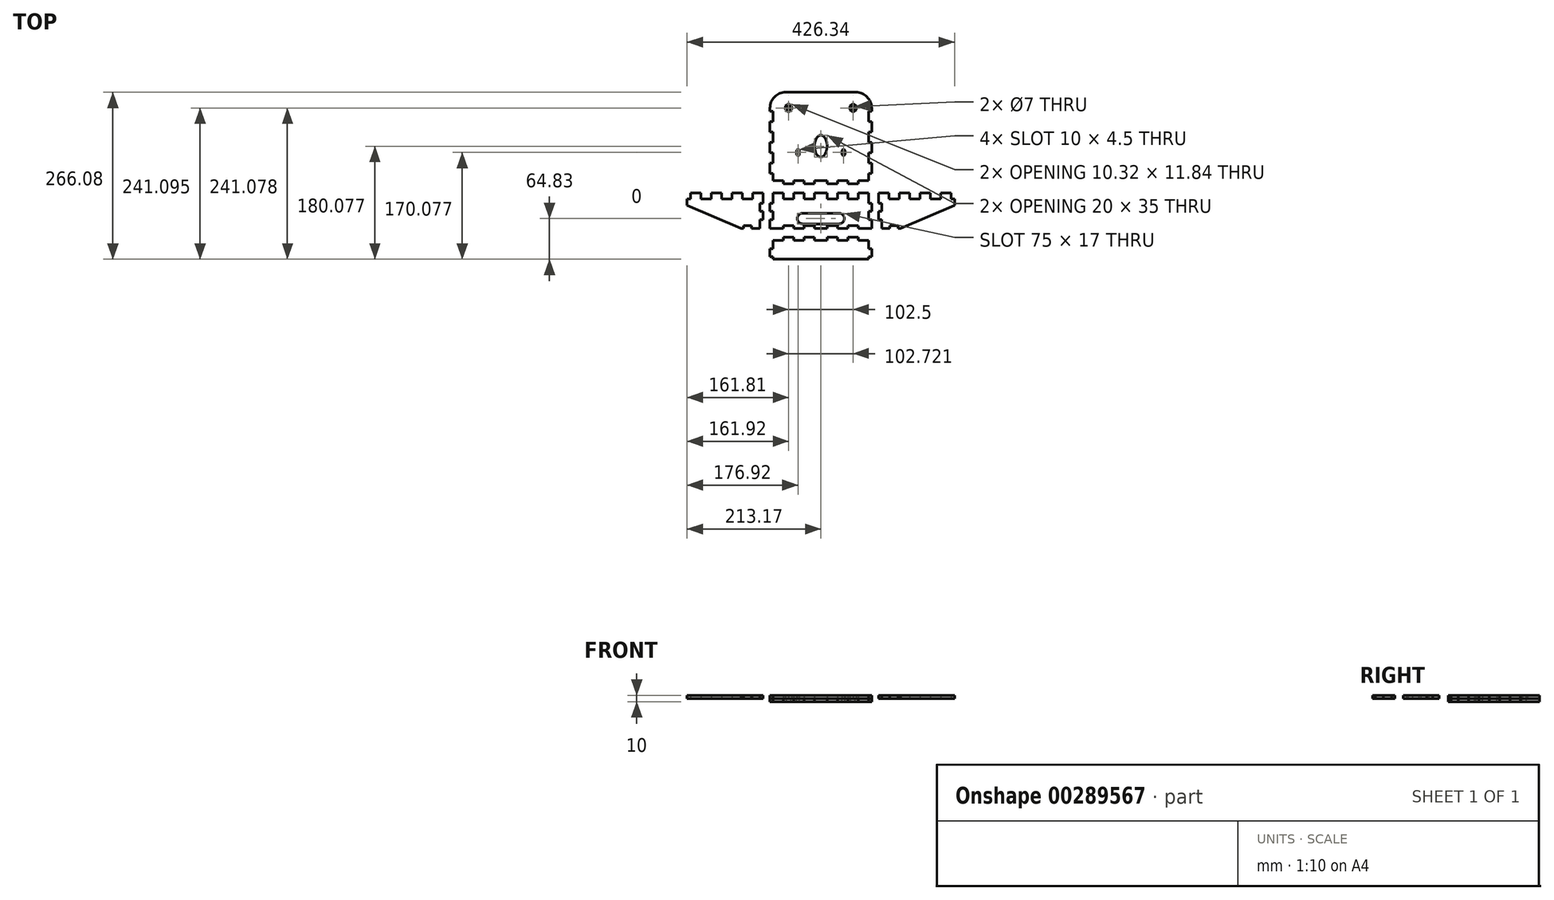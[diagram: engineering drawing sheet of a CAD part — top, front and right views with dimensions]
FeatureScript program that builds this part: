
annotation { "Feature Type Name" : "Feature", "Feature Type Description" : "" }
export const myFeature = defineFeature(function(context is Context, id is Id, definition is map)
    precondition{}
    {
        {
            assignVariable(context, id + "F0", {"name" : "plywoodThickness", "anyValue" : 5});
        }
        {
            var Q0;
            Q0=qCreatedBy(makeId("Top.planeOp"),FACE);
            var sketch = newSketch(context, id + "F1", { "sketchPlane" : qUnion([Q0])});
            skLineSegment(sketch, "E0.top", {"start": v(76, 28.5) * mm, "end": v(59.5, 28.5) * mm});
            skLineSegment(sketch, "E0.left", {"start": v(81, -28.5) * mm, "end": v(81, -14) * mm});
            skPoint(sketch, "E0.middle", {"position": v(0, 0) * mm});
            skLineSegment(sketch, "E1", {"start": v(0, -28.5) * mm, "end": v(0, -21) * mm, "construction": true});
            skLineSegment(sketch, "E2", {"start": v(0, -21) * mm, "end": v(29, -21) * mm});
            skLineSegment(sketch, "E3", {"start": v(37.5, -12.5) * mm, "end": v(37.5, -12.5) * mm});
            skLineSegment(sketch, "E4", {"start": v(29, -4) * mm, "end": v(0, -4) * mm});
            skPoint(sketch, "E5.visualSharp", {"position": v(37.5, -4) * mm});
            skArc(sketch, "E5.filletArc", {"start": v(37.5, -12.5) * mm, "mid": v(35.01, -6.49) * mm, "end": v(29, -4) * mm});
            skPoint(sketch, "E6.visualSharp", {"position": v(37.5, -21) * mm});
            skArc(sketch, "E6.filletArc", {"start": v(29, -21) * mm, "mid": v(35.01, -18.51) * mm, "end": v(37.5, -12.5) * mm});
            skLineSegment(sketch, "E7", {"start": v(59.5, -42.33) * mm, "end": v(43, -42.33) * mm});
            skLineSegment(sketch, "E8", {"start": v(81, -60.33) * mm, "end": v(81, -73.33) * mm});
            skLineSegment(sketch, "E9", {"start": v(76, -77.33) * mm, "end": v(0, -77.33) * mm});
            skLineSegment(sketch, "E10", {"start": v(92.17, -14) * mm, "end": v(92.17, -1) * mm});
            skLineSegment(sketch, "E11", {"start": v(97.17, -28.5) * mm, "end": v(110.17, -28.5) * mm});
            skPoint(sketch, "E12", {"position": v(0, 28.5) * mm});
            skLineSegment(sketch, "E13", {"start": v(59.5, 42.75) * mm, "end": v(43, 42.75) * mm});
            skLineSegment(sketch, "E14", {"start": v(81, 59.25) * mm, "end": v(81, 75.75) * mm});
            skLineSegment(sketch, "E15", {"start": v(56, 188.75) * mm, "end": v(0, 188.75) * mm});
            skLineSegment(sketch, "E16", {"start": v(59.5, 28.5) * mm, "end": v(59.5, 18.5) * mm});
            skLineSegment(sketch, "E17", {"start": v(59.5, 18.5) * mm, "end": v(43, 18.5) * mm});
            skLineSegment(sketch, "E18", {"start": v(43, 18.5) * mm, "end": v(43, 28.5) * mm});
            skLineSegment(sketch, "E19.trimOffspring", {"start": v(43, 28.5) * mm, "end": v(26.5, 28.5) * mm});
            skLineSegment(sketch, "E20", {"start": v(76, 28.5) * mm, "end": v(76, 18.5) * mm});
            skLineSegment(sketch, "E21.1.0.1", {"start": v(26.5, 28.5) * mm, "end": v(26.5, 18.5) * mm});
            skLineSegment(sketch, "E21.1.0.2", {"start": v(26.5, 18.5) * mm, "end": v(10, 18.5) * mm});
            skLineSegment(sketch, "E21.1.0.3", {"start": v(10, 18.5) * mm, "end": v(10, 28.5) * mm});
            skLineSegment(sketch, "E21.direction1", {"start": v(43, 18.5) * mm, "end": v(10, 18.5) * mm, "construction": true});
            skLineSegment(sketch, "E22.trimOffspring", {"start": v(10, 28.5) * mm, "end": v(0, 28.5) * mm});
            skLineSegment(sketch, "E23", {"start": v(59.5, 42.75) * mm, "end": v(59.5, 47.75) * mm});
            skLineSegment(sketch, "E24", {"start": v(59.5, 47.75) * mm, "end": v(76, 47.75) * mm});
            skLineSegment(sketch, "E25", {"start": v(43, 42.75) * mm, "end": v(43, 47.75) * mm});
            skLineSegment(sketch, "E26", {"start": v(43, 47.75) * mm, "end": v(26.5, 47.75) * mm});
            skLineSegment(sketch, "E27", {"start": v(26.5, 47.75) * mm, "end": v(26.5, 42.75) * mm});
            skLineSegment(sketch, "E28", {"start": v(26.5, 42.75) * mm, "end": v(10, 42.75) * mm});
            skLineSegment(sketch, "E29", {"start": v(10, 42.75) * mm, "end": v(10, 47.75) * mm});
            skLineSegment(sketch, "E30", {"start": v(10, 47.75) * mm, "end": v(0, 47.75) * mm});
            skLineSegment(sketch, "E31", {"start": v(76, 47.75) * mm, "end": v(76, 59.25) * mm});
            skLineSegment(sketch, "E32", {"start": v(76, 59.25) * mm, "end": v(81, 59.25) * mm});
            skLineSegment(sketch, "E33", {"start": v(81, 188.75) * mm, "end": v(81, 163.75) * mm, "construction": true});
            skLineSegment(sketch, "E34", {"start": v(81, 75.75) * mm, "end": v(76, 75.75) * mm});
            skLineSegment(sketch, "E35", {"start": v(76, 75.75) * mm, "end": v(76, 92.25) * mm});
            skLineSegment(sketch, "E36", {"start": v(76, 59.25) * mm, "end": v(76, 75.75) * mm, "construction": true});
            skLineSegment(sketch, "E37", {"start": v(76, 92.25) * mm, "end": v(81, 92.25) * mm});
            skLineSegment(sketch, "E38.trimOffspring", {"start": v(81, 92.25) * mm, "end": v(81, 108.75) * mm});
            skLineSegment(sketch, "E39.0.1.1", {"start": v(81, 108.75) * mm, "end": v(76, 108.75) * mm});
            skLineSegment(sketch, "E39.0.1.2", {"start": v(76, 108.75) * mm, "end": v(76, 125.25) * mm});
            skLineSegment(sketch, "E39.0.1.3", {"start": v(76, 125.25) * mm, "end": v(81, 125.25) * mm});
            skLineSegment(sketch, "E39.0.2.0", {"start": v(81, 125.25) * mm, "end": v(81, 141.75) * mm});
            skLineSegment(sketch, "E39.0.2.1", {"start": v(81, 141.75) * mm, "end": v(76, 141.75) * mm});
            skLineSegment(sketch, "E39.0.2.2", {"start": v(76, 141.75) * mm, "end": v(76, 158.25) * mm});
            skLineSegment(sketch, "E39.0.2.3", {"start": v(76, 158.25) * mm, "end": v(81, 158.25) * mm});
            skLineSegment(sketch, "E39.direction1", {"start": v(81, 59.25) * mm, "end": v(106, 59.25) * mm, "construction": true});
            skLineSegment(sketch, "E39.direction2", {"start": v(81, 59.25) * mm, "end": v(81, 92.25) * mm, "construction": true});
            skLineSegment(sketch, "E40.trimOffspring", {"start": v(81, 158.25) * mm, "end": v(81, 163.75) * mm});
            skLineSegment(sketch, "E41", {"start": v(92.17, 28.5) * mm, "end": v(108.67, 28.5) * mm});
            skLineSegment(sketch, "E42", {"start": v(108.67, 28.5) * mm, "end": v(108.67, 18.5) * mm});
            skLineSegment(sketch, "E43", {"start": v(108.67, 18.5) * mm, "end": v(125.17, 18.5) * mm});
            skLineSegment(sketch, "E44", {"start": v(125.17, 18.5) * mm, "end": v(125.17, 28.5) * mm});
            skLineSegment(sketch, "E45", {"start": v(97.17, -28.5) * mm, "end": v(110.17, -28.5) * mm, "construction": true});
            skLineSegment(sketch, "E46", {"start": v(213.17, -28.5) * mm, "end": v(213.17, 18.5) * mm, "construction": true});
            skLineSegment(sketch, "E47.1.0.0", {"start": v(158.17, 18.5) * mm, "end": v(158.17, 28.5) * mm});
            skLineSegment(sketch, "E47.1.0.1", {"start": v(125.17, 28.5) * mm, "end": v(141.67, 28.5) * mm});
            skLineSegment(sketch, "E47.1.0.2", {"start": v(141.67, 18.5) * mm, "end": v(158.17, 18.5) * mm});
            skLineSegment(sketch, "E47.1.0.3", {"start": v(141.67, 28.5) * mm, "end": v(141.67, 18.5) * mm});
            skLineSegment(sketch, "E47.2.0.0", {"start": v(191.17, 18.5) * mm, "end": v(191.17, 28.5) * mm});
            skLineSegment(sketch, "E47.2.0.1", {"start": v(158.17, 28.5) * mm, "end": v(174.67, 28.5) * mm});
            skLineSegment(sketch, "E47.2.0.2", {"start": v(174.67, 18.5) * mm, "end": v(191.17, 18.5) * mm});
            skLineSegment(sketch, "E47.2.0.3", {"start": v(174.67, 28.5) * mm, "end": v(174.67, 18.5) * mm});
            skLineSegment(sketch, "E47.3.0.1", {"start": v(191.17, 28.5) * mm, "end": v(207.67, 28.5) * mm});
            skLineSegment(sketch, "E47.3.0.2", {"start": v(207.67, 18.5) * mm, "end": v(213.17, 18.5) * mm});
            skLineSegment(sketch, "E47.3.0.3", {"start": v(207.67, 28.5) * mm, "end": v(207.67, 18.5) * mm});
            skLineSegment(sketch, "E47.direction1", {"start": v(92.17, 28.5) * mm, "end": v(125.17, 28.5) * mm, "construction": true});
            skLineSegment(sketch, "E48", {"start": v(213.17, 18.5) * mm, "end": v(213.17, 8.5) * mm});
            skLineSegment(sketch, "E49", {"start": v(213.17, 8.5) * mm, "end": v(127.17, -28.5) * mm});
            skLineSegment(sketch, "E50", {"start": v(76, 28.5) * mm, "end": v(76, 12) * mm});
            skLineSegment(sketch, "E51", {"start": v(76, 12) * mm, "end": v(81, 12) * mm});
            skLineSegment(sketch, "E52", {"start": v(92.17, 12) * mm, "end": v(97.17, 12) * mm});
            skLineSegment(sketch, "E53", {"start": v(97.17, 12) * mm, "end": v(97.17, -1) * mm});
            skLineSegment(sketch, "E54", {"start": v(97.17, -1) * mm, "end": v(92.17, -1) * mm});
            skLineSegment(sketch, "E55.trimOffspring", {"start": v(92.17, 12) * mm, "end": v(92.17, 28.5) * mm});
            skLineSegment(sketch, "E56", {"start": v(81, -1) * mm, "end": v(76, -1) * mm});
            skLineSegment(sketch, "E57", {"start": v(76, -1) * mm, "end": v(76, -14) * mm});
            skLineSegment(sketch, "E58", {"start": v(76, -14) * mm, "end": v(81, -14) * mm});
            skLineSegment(sketch, "E59.trimOffspring", {"start": v(81, -1) * mm, "end": v(81, 12) * mm});
            skLineSegment(sketch, "E60", {"start": v(92.17, -14) * mm, "end": v(97.17, -14) * mm});
            skLineSegment(sketch, "E61", {"start": v(97.17, -14) * mm, "end": v(97.17, -28.5) * mm});
            skLineSegment(sketch, "E62", {"start": v(110.17, -28.5) * mm, "end": v(110.17, -23.5) * mm});
            skLineSegment(sketch, "E63", {"start": v(110.17, -23.5) * mm, "end": v(123.17, -23.5) * mm});
            skLineSegment(sketch, "E64", {"start": v(123.17, -23.5) * mm, "end": v(123.17, -28.5) * mm});
            skLineSegment(sketch, "E65.trimOffspring", {"start": v(123.17, -28.5) * mm, "end": v(213.17, -28.5) * mm, "construction": true});
            skLineSegment(sketch, "E66.trimOffspring", {"start": v(123.17, -28.5) * mm, "end": v(127.17, -28.5) * mm});
            skLineSegment(sketch, "E67", {"start": v(76, -47.33) * mm, "end": v(76, -60.33) * mm});
            skLineSegment(sketch, "E68", {"start": v(76, -60.33) * mm, "end": v(81, -60.33) * mm});
            skLineSegment(sketch, "E69", {"start": v(81, -73.33) * mm, "end": v(76, -73.33) * mm});
            skLineSegment(sketch, "E70", {"start": v(76, -73.33) * mm, "end": v(76, -77.33) * mm});
            skLineSegment(sketch, "E71", {"start": v(59.5, -28.5) * mm, "end": v(59.5, -23.5) * mm});
            skLineSegment(sketch, "E72", {"start": v(59.5, -23.5) * mm, "end": v(43, -23.5) * mm});
            skLineSegment(sketch, "E73", {"start": v(43, -23.5) * mm, "end": v(43, -28.5) * mm});
            skLineSegment(sketch, "E74", {"start": v(26.5, -28.5) * mm, "end": v(26.5, -23.5) * mm});
            skLineSegment(sketch, "E75", {"start": v(26.5, -23.5) * mm, "end": v(10, -23.5) * mm});
            skLineSegment(sketch, "E76", {"start": v(10, -23.5) * mm, "end": v(10, -28.5) * mm});
            skLineSegment(sketch, "E77.trimOffspring", {"start": v(43, -28.5) * mm, "end": v(26.5, -28.5) * mm});
            skLineSegment(sketch, "E78.trimOffspring", {"start": v(10, -28.5) * mm, "end": v(0, -28.5) * mm});
            skLineSegment(sketch, "E79", {"start": v(59.5, -28.5) * mm, "end": v(81, -28.5) * mm});
            skLineSegment(sketch, "E80", {"start": v(59.5, -42.33) * mm, "end": v(59.5, -47.33) * mm});
            skLineSegment(sketch, "E81", {"start": v(59.5, -47.33) * mm, "end": v(76, -47.33) * mm});
            skLineSegment(sketch, "E82", {"start": v(43, -42.33) * mm, "end": v(43, -47.33) * mm});
            skLineSegment(sketch, "E83", {"start": v(43, -47.33) * mm, "end": v(26.5, -47.33) * mm});
            skLineSegment(sketch, "E84", {"start": v(26.5, -47.33) * mm, "end": v(26.5, -42.33) * mm});
            skLineSegment(sketch, "E85", {"start": v(10, -42.33) * mm, "end": v(10, -47.33) * mm});
            skLineSegment(sketch, "E86", {"start": v(10, -47.33) * mm, "end": v(0, -47.33) * mm});
            skLineSegment(sketch, "E87.trimOffspring", {"start": v(26.5, -42.33) * mm, "end": v(10, -42.33) * mm});
            skLineSegment(sketch, "E88", {"start": v(0, -85.94) * mm, "end": v(0, 158.23) * mm, "construction": true});
            skLineSegment(sketch, "E89.MirrorCS", {"start": v(-76, 59.25) * mm, "end": v(-81, 59.25) * mm});
            skLineSegment(sketch, "E90.MirrorCS", {"start": v(-76, 92.25) * mm, "end": v(-81, 92.25) * mm});
            skLineSegment(sketch, "E91.MirrorCS", {"start": v(-59.5, 42.75) * mm, "end": v(-59.5, 47.75) * mm});
            skLineSegment(sketch, "E92.MirrorCS", {"start": v(-43, 42.75) * mm, "end": v(-43, 47.75) * mm});
            skLineSegment(sketch, "E93.MirrorCS", {"start": v(-81, 108.75) * mm, "end": v(-76, 108.75) * mm});
            skLineSegment(sketch, "E94.MirrorCS", {"start": v(-59.5, -28.5) * mm, "end": v(-59.5, -23.5) * mm});
            skLineSegment(sketch, "E95.MirrorCS", {"start": v(-76, -73.33) * mm, "end": v(-76, -77.33) * mm});
            skLineSegment(sketch, "E96.MirrorCS", {"start": v(-76, 158.25) * mm, "end": v(-81, 158.25) * mm});
            skLineSegment(sketch, "E97.MirrorCS", {"start": v(-10, -42.33) * mm, "end": v(-10, -47.33) * mm});
            skLineSegment(sketch, "E98.MirrorCS", {"start": v(-81, -73.33) * mm, "end": v(-76, -73.33) * mm});
            skLineSegment(sketch, "E99.MirrorCS", {"start": v(-81, -1) * mm, "end": v(-76, -1) * mm});
            skLineSegment(sketch, "E100.MirrorCS", {"start": v(-10, 42.75) * mm, "end": v(-10, 47.75) * mm});
            skLineSegment(sketch, "E101.MirrorCS", {"start": v(-81, 141.75) * mm, "end": v(-76, 141.75) * mm});
            skLineSegment(sketch, "E102.MirrorCS", {"start": v(-76, -14) * mm, "end": v(-81, -14) * mm});
            skLineSegment(sketch, "E103.MirrorCS", {"start": v(-43, -42.33) * mm, "end": v(-43, -47.33) * mm});
            skLineSegment(sketch, "E104.MirrorCS", {"start": v(-81, -60.33) * mm, "end": v(-81, -73.33) * mm});
            skLineSegment(sketch, "E105.MirrorCS", {"start": v(-43, -23.5) * mm, "end": v(-43, -28.5) * mm});
            skLineSegment(sketch, "E106.MirrorCS", {"start": v(-26.5, 47.75) * mm, "end": v(-26.5, 42.75) * mm});
            skLineSegment(sketch, "E107.MirrorCS", {"start": v(-76, 12) * mm, "end": v(-81, 12) * mm});
            skLineSegment(sketch, "E108.MirrorCS", {"start": v(-26.5, -28.5) * mm, "end": v(-26.5, -23.5) * mm});
            skLineSegment(sketch, "E109.MirrorCS", {"start": v(-59.5, -42.33) * mm, "end": v(-59.5, -47.33) * mm});
            skLineSegment(sketch, "E110.MirrorCS", {"start": v(-76, 125.25) * mm, "end": v(-81, 125.25) * mm});
            skLineSegment(sketch, "E111.MirrorCS", {"start": v(-76, -60.33) * mm, "end": v(-81, -60.33) * mm});
            skLineSegment(sketch, "E112.MirrorCS", {"start": v(-10, -23.5) * mm, "end": v(-10, -28.5) * mm});
            skLineSegment(sketch, "E113.MirrorCS", {"start": v(-26.5, -47.33) * mm, "end": v(-26.5, -42.33) * mm});
            skLineSegment(sketch, "E114.MirrorCS", {"start": v(-81, 75.75) * mm, "end": v(-76, 75.75) * mm});
            skLineSegment(sketch, "E115.MirrorCS", {"start": v(-81, 92.25) * mm, "end": v(-81, 108.75) * mm});
            skLineSegment(sketch, "E116.MirrorCS", {"start": v(-76, 28.5) * mm, "end": v(-76, 18.5) * mm});
            skLineSegment(sketch, "E117.MirrorCS", {"start": v(-81, 59.25) * mm, "end": v(-81, 75.75) * mm});
            skLineSegment(sketch, "E118.MirrorCS", {"start": v(-81, 158.25) * mm, "end": v(-81, 163.75) * mm});
            skLineSegment(sketch, "E119.MirrorCS", {"start": v(-76, 28.5) * mm, "end": v(-59.5, 28.5) * mm});
            skLineSegment(sketch, "E120.MirrorCS", {"start": v(-81, 125.25) * mm, "end": v(-81, 141.75) * mm});
            skLineSegment(sketch, "E121.MirrorCS", {"start": v(-43, 28.5) * mm, "end": v(-26.5, 28.5) * mm});
            skLineSegment(sketch, "E122.MirrorCS", {"start": v(-26.5, 42.75) * mm, "end": v(-10, 42.75) * mm});
            skLineSegment(sketch, "E123.MirrorCS", {"start": v(-26.5, 18.5) * mm, "end": v(-10, 18.5) * mm});
            skLineSegment(sketch, "E124.MirrorCS", {"start": v(-76, 28.5) * mm, "end": v(-76, 12) * mm});
            skLineSegment(sketch, "E125.MirrorCS", {"start": v(-76, -1) * mm, "end": v(-76, -14) * mm});
            skLineSegment(sketch, "E126.MirrorCS", {"start": v(-10, -28.5) * mm, "end": v(0, -28.5) * mm});
            skLineSegment(sketch, "E127.MirrorCS", {"start": v(-10, 28.5) * mm, "end": v(0, 28.5) * mm});
            skPoint(sketch, "E128.MirrorP", {"position": v(-37.5, -4) * mm});
            skLineSegment(sketch, "E129.MirrorCS", {"start": v(-59.5, -28.5) * mm, "end": v(-81, -28.5) * mm});
            skLineSegment(sketch, "E130.MirrorCS", {"start": v(-81, 59.25) * mm, "end": v(-106, 59.25) * mm, "construction": true});
            skLineSegment(sketch, "E131.MirrorCS", {"start": v(-76, 47.75) * mm, "end": v(-76, 59.25) * mm});
            skLineSegment(sketch, "E132.MirrorCS", {"start": v(-59.5, -47.33) * mm, "end": v(-76, -47.33) * mm});
            skLineSegment(sketch, "E133.MirrorCS", {"start": v(-59.5, 47.75) * mm, "end": v(-76, 47.75) * mm});
            skLineSegment(sketch, "E134.MirrorCS", {"start": v(-59.5, -23.5) * mm, "end": v(-43, -23.5) * mm});
            skLineSegment(sketch, "E135.MirrorCS", {"start": v(-43, 18.5) * mm, "end": v(-43, 28.5) * mm});
            skLineSegment(sketch, "E136.MirrorCS", {"start": v(-43, -28.5) * mm, "end": v(-26.5, -28.5) * mm});
            skLineSegment(sketch, "E137.MirrorCS", {"start": v(-76, 59.25) * mm, "end": v(-76, 75.75) * mm, "construction": true});
            skLineSegment(sketch, "E138.MirrorCS", {"start": v(-43, 18.5) * mm, "end": v(-10, 18.5) * mm, "construction": true});
            skLineSegment(sketch, "E139.MirrorCS", {"start": v(-76, -77.33) * mm, "end": v(0, -77.33) * mm});
            skArc(sketch, "E140.MirrorCS", {"start": v(-29, -21) * mm, "mid": v(-35.01, -18.51) * mm, "end": v(-37.5, -12.5) * mm});
            skLineSegment(sketch, "E141.MirrorCS", {"start": v(-10, 47.75) * mm, "end": v(0, 47.75) * mm});
            skLineSegment(sketch, "E142.MirrorCS", {"start": v(-10, -47.33) * mm, "end": v(0, -47.33) * mm});
            skLineSegment(sketch, "E143.MirrorCS", {"start": v(-29, -4) * mm, "end": v(0, -4) * mm});
            skLineSegment(sketch, "E144.MirrorCS", {"start": v(0, -21) * mm, "end": v(-29, -21) * mm});
            skLineSegment(sketch, "E145.MirrorCS", {"start": v(-76, 141.75) * mm, "end": v(-76, 158.25) * mm});
            skLineSegment(sketch, "E146.MirrorCS", {"start": v(-59.5, 28.5) * mm, "end": v(-59.5, 18.5) * mm});
            skLineSegment(sketch, "E147.MirrorCS", {"start": v(-59.5, 18.5) * mm, "end": v(-43, 18.5) * mm});
            skLineSegment(sketch, "E148.MirrorCS", {"start": v(-10, 18.5) * mm, "end": v(-10, 28.5) * mm});
            skLineSegment(sketch, "E149.MirrorCS", {"start": v(-56, 188.75) * mm, "end": v(0, 188.75) * mm});
            skLineSegment(sketch, "E150.MirrorCS", {"start": v(-76, -47.33) * mm, "end": v(-76, -60.33) * mm});
            skLineSegment(sketch, "E151.MirrorCS", {"start": v(-43, 47.75) * mm, "end": v(-26.5, 47.75) * mm});
            skLineSegment(sketch, "E152.MirrorCS", {"start": v(-81, 188.75) * mm, "end": v(-81, 163.75) * mm, "construction": true});
            skLineSegment(sketch, "E153.MirrorCS", {"start": v(-43, -47.33) * mm, "end": v(-26.5, -47.33) * mm});
            skLineSegment(sketch, "E154.MirrorCS", {"start": v(-59.5, 42.75) * mm, "end": v(-43, 42.75) * mm});
            skLineSegment(sketch, "E155.MirrorCS", {"start": v(-81, -1) * mm, "end": v(-81, 12) * mm});
            skLineSegment(sketch, "E156.MirrorCS", {"start": v(-26.5, 28.5) * mm, "end": v(-26.5, 18.5) * mm});
            skLineSegment(sketch, "E157.MirrorCS", {"start": v(-26.5, -42.33) * mm, "end": v(-10, -42.33) * mm});
            skLineSegment(sketch, "E158.MirrorCS", {"start": v(-81, 59.25) * mm, "end": v(-81, 92.25) * mm, "construction": true});
            skLineSegment(sketch, "E159.MirrorCS", {"start": v(-81, -28.5) * mm, "end": v(-81, -14) * mm});
            skArc(sketch, "E160.MirrorCS", {"start": v(-37.5, -12.5) * mm, "mid": v(-35.01, -6.49) * mm, "end": v(-29, -4) * mm});
            skLineSegment(sketch, "E161.MirrorCS", {"start": v(-26.5, -23.5) * mm, "end": v(-10, -23.5) * mm});
            skLineSegment(sketch, "E162.MirrorCS", {"start": v(-76, 75.75) * mm, "end": v(-76, 92.25) * mm});
            skLineSegment(sketch, "E163.MirrorCS", {"start": v(-37.5, -12.5) * mm, "end": v(-37.5, -12.5) * mm});
            skPoint(sketch, "E164.MirrorP", {"position": v(-37.5, -21) * mm});
            skLineSegment(sketch, "E165.MirrorCS", {"start": v(-59.5, -42.33) * mm, "end": v(-43, -42.33) * mm});
            skLineSegment(sketch, "E166.MirrorCS", {"start": v(-76, 108.75) * mm, "end": v(-76, 125.25) * mm});
            skLineSegment(sketch, "E167.MirrorCS", {"start": v(-97.17, -1) * mm, "end": v(-92.17, -1) * mm});
            skLineSegment(sketch, "E168.MirrorCS", {"start": v(-92.17, 12) * mm, "end": v(-97.17, 12) * mm});
            skLineSegment(sketch, "E169.MirrorCS", {"start": v(-123.17, -28.5) * mm, "end": v(-127.17, -28.5) * mm});
            skLineSegment(sketch, "E170.MirrorCS", {"start": v(-110.17, -28.5) * mm, "end": v(-110.17, -23.5) * mm});
            skLineSegment(sketch, "E171.MirrorCS", {"start": v(-97.17, -28.5) * mm, "end": v(-110.17, -28.5) * mm});
            skLineSegment(sketch, "E172.MirrorCS", {"start": v(-123.17, -23.5) * mm, "end": v(-123.17, -28.5) * mm});
            skLineSegment(sketch, "E173.MirrorCS", {"start": v(-207.67, 18.5) * mm, "end": v(-213.17, 18.5) * mm});
            skLineSegment(sketch, "E174.MirrorCS", {"start": v(-92.17, -14) * mm, "end": v(-97.17, -14) * mm});
            skLineSegment(sketch, "E175.MirrorCS", {"start": v(-92.17, 28.5) * mm, "end": v(-108.67, 28.5) * mm});
            skLineSegment(sketch, "E176.MirrorCS", {"start": v(-213.17, 18.5) * mm, "end": v(-213.17, 8.5) * mm});
            skLineSegment(sketch, "E177.MirrorCS", {"start": v(-158.17, 28.5) * mm, "end": v(-174.67, 28.5) * mm});
            skLineSegment(sketch, "E178.MirrorCS", {"start": v(-191.17, 18.5) * mm, "end": v(-191.17, 28.5) * mm});
            skLineSegment(sketch, "E179.MirrorCS", {"start": v(-92.17, -14) * mm, "end": v(-92.17, -1) * mm});
            skLineSegment(sketch, "E180.MirrorCS", {"start": v(-141.67, 28.5) * mm, "end": v(-141.67, 18.5) * mm});
            skLineSegment(sketch, "E181.MirrorCS", {"start": v(-92.17, 12) * mm, "end": v(-92.17, 28.5) * mm});
            skLineSegment(sketch, "E182.MirrorCS", {"start": v(-141.67, 18.5) * mm, "end": v(-158.17, 18.5) * mm});
            skLineSegment(sketch, "E183.MirrorCS", {"start": v(-125.17, 28.5) * mm, "end": v(-141.67, 28.5) * mm});
            skLineSegment(sketch, "E184.MirrorCS", {"start": v(-97.17, 12) * mm, "end": v(-97.17, -1) * mm});
            skLineSegment(sketch, "E185.MirrorCS", {"start": v(-158.17, 18.5) * mm, "end": v(-158.17, 28.5) * mm});
            skLineSegment(sketch, "E186.MirrorCS", {"start": v(-108.67, 28.5) * mm, "end": v(-108.67, 18.5) * mm});
            skLineSegment(sketch, "E187.MirrorCS", {"start": v(-207.67, 28.5) * mm, "end": v(-207.67, 18.5) * mm});
            skLineSegment(sketch, "E188.MirrorCS", {"start": v(-174.67, 18.5) * mm, "end": v(-191.17, 18.5) * mm});
            skLineSegment(sketch, "E189.MirrorCS", {"start": v(-92.17, 28.5) * mm, "end": v(-125.17, 28.5) * mm, "construction": true});
            skLineSegment(sketch, "E190.MirrorCS", {"start": v(-213.17, -28.5) * mm, "end": v(-213.17, 18.5) * mm, "construction": true});
            skLineSegment(sketch, "E191.MirrorCS", {"start": v(-191.17, 28.5) * mm, "end": v(-207.67, 28.5) * mm});
            skLineSegment(sketch, "E192.MirrorCS", {"start": v(-110.17, -23.5) * mm, "end": v(-123.17, -23.5) * mm});
            skLineSegment(sketch, "E193.MirrorCS", {"start": v(-108.67, 18.5) * mm, "end": v(-125.17, 18.5) * mm});
            skLineSegment(sketch, "E194.MirrorCS", {"start": v(-97.17, -28.5) * mm, "end": v(-110.17, -28.5) * mm, "construction": true});
            skLineSegment(sketch, "E195.MirrorCS", {"start": v(-174.67, 28.5) * mm, "end": v(-174.67, 18.5) * mm});
            skLineSegment(sketch, "E196.MirrorCS", {"start": v(-125.17, 18.5) * mm, "end": v(-125.17, 28.5) * mm});
            skLineSegment(sketch, "E197.MirrorCS", {"start": v(-97.17, -14) * mm, "end": v(-97.17, -28.5) * mm});
            skLineSegment(sketch, "E198.MirrorCS", {"start": v(-123.17, -28.5) * mm, "end": v(-213.17, -28.5) * mm, "construction": true});
            skLineSegment(sketch, "E199.MirrorCS", {"start": v(-213.17, 8.5) * mm, "end": v(-127.17, -28.5) * mm});
            skLineSegment(sketch, "E200", {"start": v(0, 188.75) * mm, "end": v(0, 163.75) * mm, "construction": true});
            skLineSegment(sketch, "E201", {"start": v(0, 163.75) * mm, "end": v(-51.25, 163.75) * mm, "construction": true});
            skCircle(sketch, "E202", {"center": v(-51.25, 163.75) * mm, "radius": 3.5 * mm});
            skLineSegment(sketch, "E203", {"start": v(-46.2, 160.85) * mm, "end": v(-46.2, 166.68) * mm});
            skLineSegment(sketch, "E204", {"start": v(-46.2, 166.68) * mm, "end": v(-51.36, 169.69) * mm});
            skLineSegment(sketch, "E205", {"start": v(-51.36, 169.69) * mm, "end": v(-56.52, 166.72) * mm});
            skLineSegment(sketch, "E206", {"start": v(-56.52, 166.72) * mm, "end": v(-56.52, 160.74) * mm});
            skLineSegment(sketch, "E207", {"start": v(-56.52, 160.74) * mm, "end": v(-51.36, 157.84) * mm});
            skLineSegment(sketch, "E208", {"start": v(-51.36, 157.84) * mm, "end": v(-46.2, 160.85) * mm});
            skLineSegment(sketch, "E209.MirrorCS", {"start": v(46.2, 166.68) * mm, "end": v(51.36, 169.69) * mm});
            skLineSegment(sketch, "E210.MirrorCS", {"start": v(51.36, 169.69) * mm, "end": v(56.52, 166.72) * mm});
            skLineSegment(sketch, "E211.MirrorCS", {"start": v(56.52, 160.74) * mm, "end": v(51.36, 157.84) * mm});
            skLineSegment(sketch, "E212.MirrorCS", {"start": v(51.36, 157.84) * mm, "end": v(46.2, 160.85) * mm});
            skCircle(sketch, "E213.MirrorC", {"center": v(51.25, 163.75) * mm, "radius": 3.5 * mm});
            skLineSegment(sketch, "E214.MirrorCS", {"start": v(56.52, 166.72) * mm, "end": v(56.52, 160.74) * mm});
            skLineSegment(sketch, "E215.MirrorCS", {"start": v(46.2, 160.85) * mm, "end": v(46.2, 166.68) * mm});
            skPoint(sketch, "E216.visualSharp", {"position": v(-81, 188.75) * mm});
            skArc(sketch, "E216.filletArc", {"start": v(-56, 188.75) * mm, "mid": v(-73.68, 181.43) * mm, "end": v(-81, 163.75) * mm});
            skPoint(sketch, "E217.visualSharp", {"position": v(81, 188.75) * mm});
            skArc(sketch, "E217.filletArc", {"start": v(81, 163.75) * mm, "mid": v(73.68, 181.43) * mm, "end": v(56, 188.75) * mm});
            skLineSegment(sketch, "E218", {"start": v(0, 47.75) * mm, "end": v(0, 102.75) * mm, "construction": true});
            skEllipse(sketch, "E219", {"center": v(0, 102.75) * mm, "majorRadius": 17.5 * mm, "minorRadius": 10 * mm, "majorAxis": v(0, -1)});
            skLineSegment(sketch, "E220", {"start": v(0, 70.3) * mm, "end": v(36.25, 70.3) * mm, "construction": true});
            skLineSegment(sketch, "E221", {"start": v(36.25, 47.75) * mm, "end": v(36.25, 92.75) * mm, "construction": true});
            skLineSegment(sketch, "E222.bottom", {"start": v(36.25, 87.75) * mm, "end": v(36.25, 87.75) * mm});
            skLineSegment(sketch, "E222.top", {"start": v(36.25, 97.75) * mm, "end": v(36.25, 97.75) * mm});
            skLineSegment(sketch, "E222.left", {"start": v(38.5, 90) * mm, "end": v(38.5, 95.5) * mm});
            skLineSegment(sketch, "E222.right", {"start": v(34, 90) * mm, "end": v(34, 95.5) * mm});
            skPoint(sketch, "E222.middle", {"position": v(36.25, 92.75) * mm});
            skPoint(sketch, "E223.visualSharp", {"position": v(38.5, 97.75) * mm});
            skArc(sketch, "E223.filletArc", {"start": v(38.5, 95.5) * mm, "mid": v(37.84, 97.09) * mm, "end": v(36.25, 97.75) * mm});
            skPoint(sketch, "E224.visualSharp", {"position": v(34, 87.75) * mm});
            skArc(sketch, "E224.filletArc", {"start": v(34, 90) * mm, "mid": v(34.66, 88.4) * mm, "end": v(36.25, 87.75) * mm});
            skPoint(sketch, "E225.visualSharp", {"position": v(38.5, 87.75) * mm});
            skArc(sketch, "E225.filletArc", {"start": v(36.25, 87.75) * mm, "mid": v(37.84, 88.4) * mm, "end": v(38.5, 90) * mm});
            skPoint(sketch, "E226.visualSharp", {"position": v(34, 97.75) * mm});
            skArc(sketch, "E226.filletArc", {"start": v(36.25, 97.75) * mm, "mid": v(34.66, 97.09) * mm, "end": v(34, 95.5) * mm});
            skArc(sketch, "E227.MirrorCS", {"start": v(-38.5, 95.5) * mm, "mid": v(-37.84, 97.09) * mm, "end": v(-36.25, 97.75) * mm});
            skPoint(sketch, "E228.MirrorP", {"position": v(-38.5, 87.75) * mm});
            skLineSegment(sketch, "E229.MirrorCS", {"start": v(-38.5, 90) * mm, "end": v(-38.5, 95.5) * mm});
            skLineSegment(sketch, "E230.MirrorCS", {"start": v(-34, 90) * mm, "end": v(-34, 95.5) * mm});
            skPoint(sketch, "E231.MirrorP", {"position": v(-34, 87.75) * mm});
            skArc(sketch, "E232.MirrorCS", {"start": v(-36.25, 87.75) * mm, "mid": v(-37.84, 88.4) * mm, "end": v(-38.5, 90) * mm});
            skArc(sketch, "E233.MirrorCS", {"start": v(-36.25, 97.75) * mm, "mid": v(-34.66, 97.09) * mm, "end": v(-34, 95.5) * mm});
            skArc(sketch, "E234.MirrorCS", {"start": v(-34, 90) * mm, "mid": v(-34.66, 88.4) * mm, "end": v(-36.25, 87.75) * mm});
            skPoint(sketch, "E235.MirrorP", {"position": v(-36.25, 92.75) * mm});
            skPoint(sketch, "E236.MirrorP", {"position": v(-38.5, 97.75) * mm});
            skPoint(sketch, "E237.MirrorP", {"position": v(-34, 97.75) * mm});
            skSolve(sketch);
        }
        {
            var Q0;
            Q0=makeQuery(id+"F1.imprint","IMPRINT",FACE,{"disambiguationData":[TD([[makeQuery(id+"F1.imprint","IMPRINT",EDGE,{"derivedFrom":sQuery(id+"F1.wireOp",EDGE,"E7")}),1.0]])]});
            var Q1;
            Q1=makeQuery(id+"F1.imprint","IMPRINT",FACE,{"disambiguationData":[TD([[makeQuery(id+"F1.imprint","IMPRINT",EDGE,{"derivedFrom":sQuery(id+"F1.wireOp",EDGE,"E10")}),-1.0]])]});
            var Q2;
            Q2=makeQuery(id+"F1.imprint","IMPRINT",FACE,{"disambiguationData":[TD([[makeQuery(id+"F1.imprint","IMPRINT",EDGE,{"derivedFrom":sQuery(id+"F1.wireOp",EDGE,"E0.left")}),1.0]])]});
            var Q3;
            Q3=makeQuery(id+"F1.imprint","IMPRINT",FACE,{"disambiguationData":[TD([[makeQuery(id+"F1.imprint","IMPRINT",EDGE,{"derivedFrom":sQuery(id+"F1.wireOp",EDGE,"E167.MirrorCS")}),-1.0]])]});
            var Q4;
            Q4=makeQuery(id+"F1.imprint","IMPRINT",FACE,{"disambiguationData":[TD([[makeQuery(id+"F1.imprint","IMPRINT",EDGE,{"derivedFrom":sQuery(id+"F1.wireOp",EDGE,"E13")}),-1.0]])]});
            extrude(context, id + "F2", {"entities" : qUnion([Q0, Q1, Q2, Q3, Q4]), "depth" : (getVariable(context, 'plywoodThickness')) * mm});
        }
        {
            var Q0;
            Q0=makeQuery(id+"F1.imprint","IMPRINT",FACE,{"disambiguationData":[TD([[makeQuery(id+"F1.imprint","IMPRINT",EDGE,{"derivedFrom":sQuery(id+"F1.wireOp",EDGE,"E13")}),-1.0]])]});
            var Q1;
            Q1=makeQuery(id+"F1.imprint","IMPRINT",FACE,{"disambiguationData":[TD([[makeQuery(id+"F1.imprint","IMPRINT",EDGE,{"derivedFrom":sQuery(id+"F1.wireOp",EDGE,"E209.MirrorCS")}),-1.0]])]});
            var Q2;
            Q2=makeQuery(id+"F1.imprint","IMPRINT",FACE,{"disambiguationData":[TD([[makeQuery(id+"F1.imprint","IMPRINT",EDGE,{"derivedFrom":sQuery(id+"F1.wireOp",EDGE,"E202")}),-1.0]])]});
            extrude(context, id + "F3", {"entities" : qUnion([Q0, Q1, Q2]), "oppositeDirection" : true, "depth" : getVariable(context, 'plywoodThickness') * mm});
        }
    });
